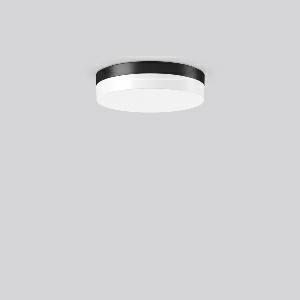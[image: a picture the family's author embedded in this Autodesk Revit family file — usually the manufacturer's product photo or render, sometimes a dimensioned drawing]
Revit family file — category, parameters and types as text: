
# Revit family: flat_slim_round_312630_0031_1_76_4615
name_source: partatom
category: Lighting Fixtures
units: mm (PartAtom-declared; Revit-internal decimal feet)

## family parameters
Cut with Voids When Loaded = No
Host = Face
Light Source = No
Part Type = Normal
Room Calculation Point = No
Round Connector Dimension = Use Diameter
Shared = No

## types (1)
- MultiLumen 1 830 (1 x LED Modul 830, 1450 lm, 3000)
    Apparent Load = 11 VA
    CIE Flux Codes = 38 68 88 84 100
    Color Rendering = 80
    Color Temperature = 3000
    Default Elevation = 1800 mm
    Height = 70 mm
    Lamp = 1 x LED Modul 830
    Lamp Light Flux = 1450 lm
    Lamp count = 1
    Length = 300 mm
    Lifetime = 50000 h
    Luminous efficacy = 132 lm/W
    Manufacturer = RZB
    ModVariant = No
    Model = 312630.0031.1.76
    Mounting Place = Ceiling
    Mounting Type = Surface mounted
    Number of Poles = 1
    OnlyDefault = Yes
    Power Factor = 1
    Product Name = FLAT SLIM round
    Product group = Surface mounted ceiling and wall luminaires
    ProductGroupID = 305
    Protection Class = Protection class I
    Protection Degree = Degree of protection
    RLX_Detail_Level = 1
    RLX_Emergency_Light_Flux = 0 lm
    RLX_Emergency_Type = 0
    RLX_Emergency_Type_DB = No
    RlxData = <blob elided: 17545 chars, md5=3be3e75e>
    Socket = socket
    Standby Power = 0 W
    System Light Flux = 1450 lm
    System Power = 11 W
    Type Comments = MultiLumen 1 830
    Type Image = 312629.0031.jpg
    URL = http://relux.com
    VarID = multilumen_1_830
    Voltage = 0 V
    Weight = 0.00 kg
    Width = 0 mm  [stored 0 ft]

note: [stored X ft] marks values corroborated as IEEE doubles in the binary element streams (Revit-internal decimal feet)

## geometry (parser evidence)
native form markers: Blend x4, Sweep x15
no freeform markers — native parametric forms only
